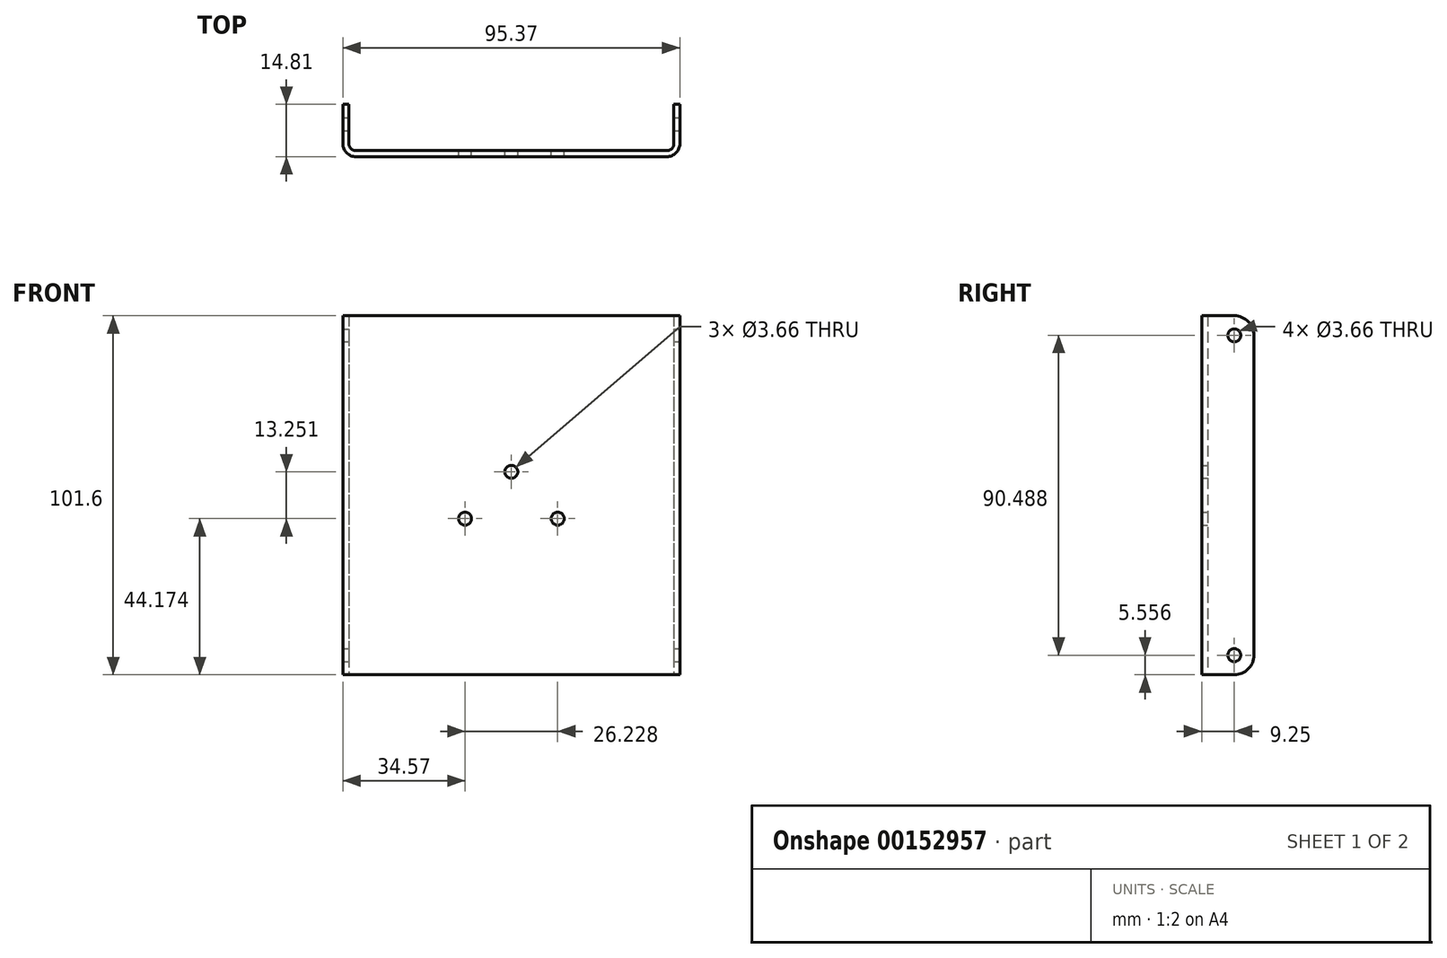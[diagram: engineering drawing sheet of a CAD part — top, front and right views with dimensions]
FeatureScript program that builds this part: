
annotation { "Feature Type Name" : "Feature", "Feature Type Description" : "" }
export const myFeature = defineFeature(function(context is Context, id is Id, definition is map)
    precondition{}
    {
        {
            var Q0;
            Q0=qCreatedBy(makeId("Top.planeOp"),FACE);
            var sketch = newSketch(context, id + "F0", { "sketchPlane" : qUnion([Q0])});
            skLineSegment(sketch, "E0.bottom", {"start": v(0, 0) * mm, "end": v(-91.95, 0) * mm});
            skLineSegment(sketch, "E0.top", {"start": v(1.7, -1.7) * mm, "end": v(-93.66, -1.7) * mm});
            skLineSegment(sketch, "E1.top", {"start": v(-91.95, 13.1) * mm, "end": v(-93.66, 13.1) * mm});
            skLineSegment(sketch, "E1.left", {"start": v(-91.95, 0) * mm, "end": v(-91.95, 13.1) * mm});
            skLineSegment(sketch, "E1.right", {"start": v(-93.66, -1.7) * mm, "end": v(-93.66, 13.1) * mm});
            skLineSegment(sketch, "E2.top", {"start": v(0, 13.1) * mm, "end": v(1.7, 13.1) * mm});
            skLineSegment(sketch, "E2.left", {"start": v(0, 0) * mm, "end": v(0, 13.1) * mm});
            skLineSegment(sketch, "E2.right", {"start": v(1.7, -1.7) * mm, "end": v(1.7, 13.1) * mm});
            skLineSegment(sketch, "E3", {"start": v(-45.98, 0) * mm, "end": v(-45.98, -1.7) * mm, "construction": true});
            skArc(sketch, "E4", {"start": v(-1.98, 0) * mm, "mid": v(-0.58, 0.58) * mm, "end": v(0, 1.98) * mm, "construction": true});
            skSolve(sketch);
        }
        {
            var Q0;
            Q0=qSketchRegion(id+"F0",true);
            extrude(context, id + "F1", {"entities" : qUnion([Q0]), "depth" : 101.6 * mm});
        }
        {
            var Q0;
            Q0=makeQuery(id+"F1.opExtrude","SWEPT_EDGE",EDGE,{"disambiguationData":[OSD([sQuery(id+"F0.wireOp",EDGE,"E0.top"),sQuery(id+"F0.wireOp",EDGE,"E2.right")])]});
            var Q1;
            Q1=makeQuery(id+"F1.opExtrude","SWEPT_EDGE",EDGE,{"disambiguationData":[OSD([sQuery(id+"F0.wireOp",EDGE,"E0.top"),sQuery(id+"F0.wireOp",EDGE,"E1.right")])]});
            var Q2;
            Q2=makeQuery(id+"FqNnmMD7oaRdpTN_1.opExtrude","CAP_EDGE",EDGE,{"disambiguationData":[OSD([sQuery(id+"FY5sMr6MULj5lJw_1.wireOp",EDGE,"W42EfhJi-fDm4-L9BW-folL-irsYfDskuzBk.top")])],"isStart":false});
            fillet(context, id + "F2", {"entities" : qUnion([Q0, Q1, Q2]), "radius" : 3.7 * mm, "tangentPropagation" : true, "allowEdgeOverflow" : false});
        }
        {
            var Q0;
            Q0=makeQuery(id+"F1.opExtrude","SWEPT_EDGE",EDGE,{"disambiguationData":[OSD([sQuery(id+"F0.wireOp",EDGE,"E0.bottom"),sQuery(id+"F0.wireOp",EDGE,"E2.left")])]});
            var Q1;
            Q1=makeQuery(id+"F1.opExtrude","SWEPT_EDGE",EDGE,{"disambiguationData":[OSD([sQuery(id+"F0.wireOp",EDGE,"E0.bottom"),sQuery(id+"F0.wireOp",EDGE,"E1.left")])]});
            fillet(context, id + "F3", {"entities" : qUnion([Q0, Q1]), "radius" : 1.98 * mm, "tangentPropagation" : true, "allowEdgeOverflow" : false});
        }
        {
            var Q0;
            Q0=makeQuery(id+"F1.opExtrude","SWEPT_FACE",FACE,{"disambiguationData":[OSD([sQuery(id+"F0.wireOp",EDGE,"E2.right")])]});
            var sketch = newSketch(context, id + "F4", { "sketchPlane" : qUnion([Q0])});
            skLineSegment(sketch, "E5.bottom", {"start": v(7.54, 101.6) * mm, "end": v(13.1, 101.6) * mm, "construction": true});
            skLineSegment(sketch, "E5.top", {"start": v(7.54, 96.04) * mm, "end": v(13.1, 96.04) * mm, "construction": true});
            skLineSegment(sketch, "E5.left", {"start": v(7.54, 101.6) * mm, "end": v(7.54, 96.04) * mm, "construction": true});
            skLineSegment(sketch, "E5.right", {"start": v(13.1, 101.6) * mm, "end": v(13.1, 96.04) * mm, "construction": true});
            skLineSegment(sketch, "E6.bottom", {"start": v(7.54, 0) * mm, "end": v(13.1, 0) * mm, "construction": true});
            skLineSegment(sketch, "E6.top", {"start": v(7.54, 5.56) * mm, "end": v(13.1, 5.56) * mm, "construction": true});
            skLineSegment(sketch, "E6.left", {"start": v(7.54, 0) * mm, "end": v(7.54, 5.56) * mm, "construction": true});
            skLineSegment(sketch, "E6.right", {"start": v(13.1, 0) * mm, "end": v(13.1, 5.56) * mm, "construction": true});
            skCircle(sketch, "E7", {"center": v(7.54, 96.04) * mm, "radius": 1.83 * mm});
            skCircle(sketch, "E8", {"center": v(7.54, 5.56) * mm, "radius": 1.83 * mm});
            skSolve(sketch);
        }
        {
            var Q0;
            Q0=qSketchRegion(id+"F4",true);
            var Q1;
            Q1=makeQuery(id+"F1.opExtrude","SWEPT_FACE",FACE,{"disambiguationData":[OSD([sQuery(id+"F0.wireOp",EDGE,"E1.right")])]});
            extrude(context, id + "F5", {"entities" : qUnion([Q0]), "operationType" : NewBodyOperationType.REMOVE, "endBound" : BoundingType.UP_TO_SURFACE, "oppositeDirection" : true, "endBoundEntityFace" : qUnion([Q1]), "depth" : 25.4 * mm});
        }
        {
            var Q0;
            Q0=makeQuery(id+"F1.opExtrude","CAP_EDGE",EDGE,{"disambiguationData":[OSD([sQuery(id+"F0.wireOp",EDGE,"E1.top")])],"isStart":false});
            var Q1;
            Q1=makeQuery(id+"F1.opExtrude","CAP_EDGE",EDGE,{"disambiguationData":[OSD([sQuery(id+"F0.wireOp",EDGE,"E1.top")])],"isStart":true});
            var Q2;
            Q2=makeQuery(id+"F1.opExtrude","CAP_EDGE",EDGE,{"disambiguationData":[OSD([sQuery(id+"F0.wireOp",EDGE,"E2.top")])],"isStart":true});
            var Q3;
            Q3=makeQuery(id+"F1.opExtrude","CAP_EDGE",EDGE,{"disambiguationData":[OSD([sQuery(id+"F0.wireOp",EDGE,"E2.top")])],"isStart":false});
            fillet(context, id + "F6", {"entities" : qUnion([Q0, Q1, Q2, Q3]), "radius" : 5.56 * mm, "tangentPropagation" : true, "allowEdgeOverflow" : false});
        }
        {
            var Q0;
            Q0=makeQuery(id+"F1.opExtrude","SWEPT_FACE",FACE,{"disambiguationData":[OSD([sQuery(id+"F0.wireOp",EDGE,"E0.bottom")])]});
            var sketch = newSketch(context, id + "F7", { "sketchPlane" : qUnion([Q0])});
            skLineSegment(sketch, "E9", {"start": v(45.98, 50.8) * mm, "end": v(59.1, 44.17) * mm, "construction": true});
            skLineSegment(sketch, "E10", {"start": v(45.98, 50.8) * mm, "end": v(32.86, 44.17) * mm, "construction": true});
            skLineSegment(sketch, "E11", {"start": v(45.98, 57.43) * mm, "end": v(59.1, 44.17) * mm, "construction": true});
            skLineSegment(sketch, "E12", {"start": v(59.1, 44.17) * mm, "end": v(32.86, 44.17) * mm, "construction": true});
            skLineSegment(sketch, "E13", {"start": v(32.86, 44.17) * mm, "end": v(45.98, 57.43) * mm, "construction": true});
            skLineSegment(sketch, "E14", {"start": v(45.98, 50.8) * mm, "end": v(45.98, 101.6) * mm, "construction": true});
            skLineSegment(sketch, "E15", {"start": v(45.98, 50.8) * mm, "end": v(45.98, 0) * mm, "construction": true});
            skCircle(sketch, "E16", {"center": v(59.1, 44.17) * mm, "radius": 1.83 * mm});
            skCircle(sketch, "E17", {"center": v(45.98, 57.43) * mm, "radius": 1.83 * mm});
            skCircle(sketch, "E18", {"center": v(32.86, 44.17) * mm, "radius": 1.83 * mm});
            skSolve(sketch);
        }
        {
            var Q0;
            Q0 = qSketchRegion(id + "F7", true);
            var Q1;
            Q1=makeQuery(id+"F1.opExtrude","SWEPT_FACE",FACE,{"disambiguationData":[OSD([sQuery(id+"F0.wireOp",EDGE,"E0.top")])]});
            extrude(context, id + "F8", {"entities" : qUnion([Q0]), "operationType" : NewBodyOperationType.REMOVE, "endBound" : BoundingType.UP_TO_SURFACE, "oppositeDirection" : true, "endBoundEntityFace" : qUnion([Q1]), "depth" : 25.4 * mm});
        }
    });
